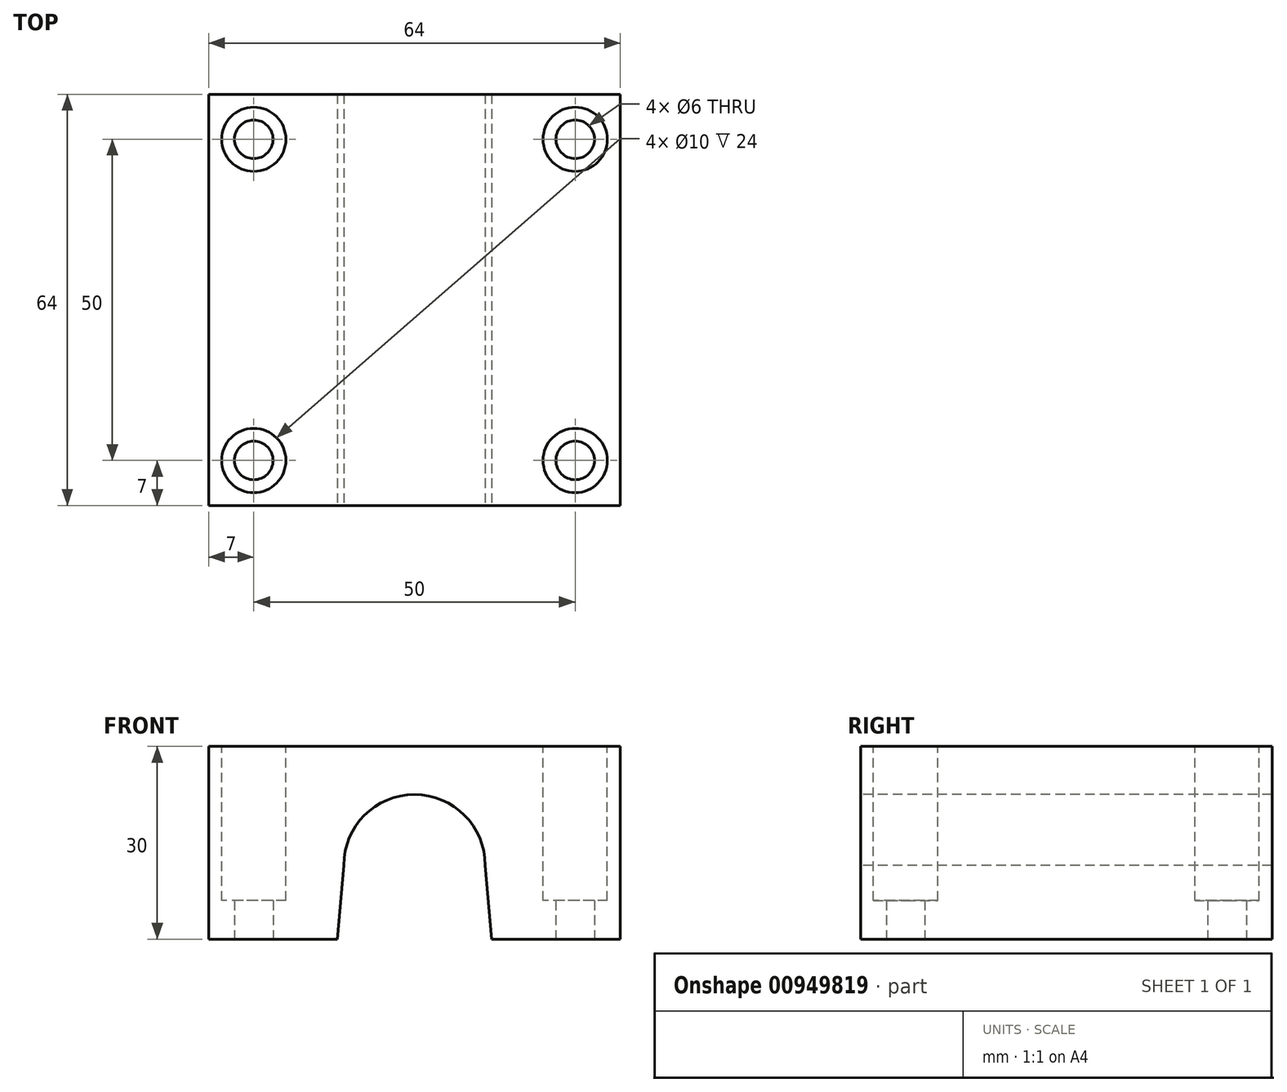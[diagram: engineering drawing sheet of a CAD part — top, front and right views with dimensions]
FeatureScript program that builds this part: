
annotation { "Feature Type Name" : "Feature", "Feature Type Description" : "" }
export const myFeature = defineFeature(function(context is Context, id is Id, definition is map)
    precondition{}
    {
        {
            var Q0;
            Q0=qCreatedBy(makeId("Top.planeOp"),FACE);
            var sketch = newSketch(context, id + "F0", { "sketchPlane" : qUnion([Q0])});
            skLineSegment(sketch, "E0.bottom", {"start": v(32, -32) * mm, "end": v(-32, -32) * mm});
            skLineSegment(sketch, "E0.top", {"start": v(32, 32) * mm, "end": v(-32, 32) * mm});
            skLineSegment(sketch, "E0.left", {"start": v(32, -32) * mm, "end": v(32, 32) * mm});
            skLineSegment(sketch, "E0.right", {"start": v(-32, -32) * mm, "end": v(-32, 32) * mm});
            skPoint(sketch, "E0.middle", {"position": v(0, 0) * mm});
            skLineSegment(sketch, "E1.bottom", {"start": v(-32, -32) * mm, "end": v(-25, -32) * mm});
            skLineSegment(sketch, "E1.top", {"start": v(-32, -25) * mm, "end": v(-25, -25) * mm});
            skLineSegment(sketch, "E1.left", {"start": v(-32, -32) * mm, "end": v(-32, -25) * mm});
            skLineSegment(sketch, "E1.right", {"start": v(-25, -32) * mm, "end": v(-25, -25) * mm});
            skLineSegment(sketch, "E2.bottom", {"start": v(32, -32) * mm, "end": v(25, -32) * mm});
            skLineSegment(sketch, "E2.top", {"start": v(32, -25) * mm, "end": v(25, -25) * mm});
            skLineSegment(sketch, "E2.left", {"start": v(32, -32) * mm, "end": v(32, -25) * mm});
            skLineSegment(sketch, "E2.right", {"start": v(25, -32) * mm, "end": v(25, -25) * mm});
            skLineSegment(sketch, "E3.bottom", {"start": v(32, 32) * mm, "end": v(25, 32) * mm});
            skLineSegment(sketch, "E3.top", {"start": v(32, 25) * mm, "end": v(25, 25) * mm});
            skLineSegment(sketch, "E3.left", {"start": v(32, 32) * mm, "end": v(32, 25) * mm});
            skLineSegment(sketch, "E3.right", {"start": v(25, 32) * mm, "end": v(25, 25) * mm});
            skLineSegment(sketch, "E4.bottom", {"start": v(-32, 32) * mm, "end": v(-25, 32) * mm});
            skLineSegment(sketch, "E4.top", {"start": v(-32, 25) * mm, "end": v(-25, 25) * mm});
            skLineSegment(sketch, "E4.left", {"start": v(-32, 32) * mm, "end": v(-32, 25) * mm});
            skLineSegment(sketch, "E4.right", {"start": v(-25, 32) * mm, "end": v(-25, 25) * mm});
            skCircle(sketch, "E5", {"center": v(-25, -25) * mm, "radius": 3 * mm});
            skCircle(sketch, "E6", {"center": v(25, -25) * mm, "radius": 3 * mm});
            skCircle(sketch, "E7", {"center": v(25, 25) * mm, "radius": 3 * mm});
            skCircle(sketch, "E8", {"center": v(-25, 25) * mm, "radius": 3 * mm});
            skLineSegment(sketch, "E9", {"start": v(-32, -32) * mm, "end": v(-12, -32) * mm});
            skLineSegment(sketch, "E10", {"start": v(32, -32) * mm, "end": v(12, -32) * mm});
            skSolve(sketch);
        }
        {
            var Q0;
            Q0 = qSketchRegion(id + "F0", true);
            var Q1;
            {var subQ18=sQuery(id+"F0.wireOp",EDGE,"E0.bottom");Q1=makeQuery(id+"F0.imprint","IMPRINT",FACE,{"disambiguationData":[TD([[makeQuery(id+"F0.imprint","IMPRINT",EDGE,{"derivedFrom":subQ18}),-1.0]])]});}
            extrude(context, id + "F1", {"entities" : qUnion([Q0, Q1]), "endBound" : BoundingType.SYMMETRIC, "depth" : 30 * mm, "offsetDistance" : 25 * mm});
        }
        {
            var Q0;
            Q0=makeQuery(id+"F1.opExtrude","SWEPT_FACE",FACE,{"disambiguationData":[OSD([sQuery(id+"F0.wireOp",EDGE,"E0.bottom"),sQuery(id+"F0.wireOp",EDGE,"E9"),sQuery(id+"F0.wireOp",EDGE,"E10")])]});
            var sketch = newSketch(context, id + "F2", { "sketchPlane" : qUnion([Q0])});
            skLineSegment(sketch, "E11", {"start": v(-32, -15) * mm, "end": v(-12, -15) * mm});
            skLineSegment(sketch, "E12", {"start": v(-12, -15) * mm, "end": v(12, -15) * mm});
            skLineSegment(sketch, "E13", {"start": v(12, -15) * mm, "end": v(32, -15) * mm});
            skLineSegment(sketch, "E14", {"start": v(0, -15) * mm, "end": v(0, 8) * mm});
            skLineSegment(sketch, "E15", {"start": v(0, 8) * mm, "end": v(0, -3.5) * mm});
            skCircle(sketch, "E16", {"center": v(0, -3.5) * mm, "radius": 11 * mm});
            skLineSegment(sketch, "E17", {"start": v(0, -3.5) * mm, "end": v(-11, -3.5) * mm});
            skLineSegment(sketch, "E18", {"start": v(0, -3.5) * mm, "end": v(11, -3.5) * mm});
            skLineSegment(sketch, "E19", {"start": v(-11, -3.5) * mm, "end": v(-12, -15) * mm});
            skLineSegment(sketch, "E20", {"start": v(11, -3.5) * mm, "end": v(12, -15) * mm});
            skSolve(sketch);
        }
        {
            var Q0;
            {var subQ0=sQuery(id+"F2.wireOp",EDGE,"E19");Q0=makeQuery(id+"F2.imprint","IMPRINT",FACE,{"disambiguationData":[TD([[makeQuery(id+"F2.imprint","IMPRINT",EDGE,{"derivedFrom":subQ0}),1.0]])]});}
            var Q1;
            {var subQ0=sQuery(id+"F2.wireOp",EDGE,"E17");Q1=makeQuery(id+"F2.imprint","IMPRINT",FACE,{"disambiguationData":[TD([[makeQuery(id+"F2.imprint","IMPRINT",EDGE,{"derivedFrom":subQ0}),1.0]])]});}
            var Q2;
            {var subQ0=sQuery(id+"F2.wireOp",EDGE,"E18");Q2=makeQuery(id+"F2.imprint","IMPRINT",FACE,{"disambiguationData":[TD([[makeQuery(id+"F2.imprint","IMPRINT",EDGE,{"derivedFrom":subQ0}),-1.0]])]});}
            var Q3;
            {var subQ0=sQuery(id+"F2.wireOp",EDGE,"E20");Q3=makeQuery(id+"F2.imprint","IMPRINT",FACE,{"disambiguationData":[TD([[makeQuery(id+"F2.imprint","IMPRINT",EDGE,{"derivedFrom":subQ0}),-1.0]])]});}
            var Q4;
            {var subQ0=sQuery(id+"F2.wireOp",EDGE,"E18");Q4=makeQuery(id+"F2.imprint","IMPRINT",FACE,{"disambiguationData":[TD([[makeQuery(id+"F2.imprint","IMPRINT",EDGE,{"derivedFrom":subQ0}),1.0]])]});}
            var Q5;
            {var subQ0=sQuery(id+"F2.wireOp",EDGE,"E17");Q5=makeQuery(id+"F2.imprint","IMPRINT",FACE,{"disambiguationData":[TD([[makeQuery(id+"F2.imprint","IMPRINT",EDGE,{"derivedFrom":subQ0}),-1.0]])]});}
            extrude(context, id + "F3", {"entities" : qUnion([Q0, Q1, Q2, Q3, Q4, Q5]), "operationType" : NewBodyOperationType.REMOVE, "oppositeDirection" : true, "depth" : 64 * mm, "offsetDistance" : 25 * mm});
        }
        {
            var Q0;
            Q0=makeQuery(id+"F1.opExtrude","CAP_FACE",FACE,{"disambiguationData":[OSD([sQuery(id+"F0.wireOp",EDGE,"E0.bottom"),sQuery(id+"F0.wireOp",EDGE,"E0.top"),sQuery(id+"F0.wireOp",EDGE,"E0.left"),sQuery(id+"F0.wireOp",EDGE,"E0.right"),sQuery(id+"F0.wireOp",EDGE,"E1.left"),sQuery(id+"F0.wireOp",EDGE,"E2.left"),sQuery(id+"F0.wireOp",EDGE,"E3.bottom"),sQuery(id+"F0.wireOp",EDGE,"E3.left"),sQuery(id+"F0.wireOp",EDGE,"E4.bottom"),sQuery(id+"F0.wireOp",EDGE,"E4.left"),sQuery(id+"F0.wireOp",EDGE,"E5"),sQuery(id+"F0.wireOp",EDGE,"E6"),sQuery(id+"F0.wireOp",EDGE,"E7"),sQuery(id+"F0.wireOp",EDGE,"E8"),sQuery(id+"F0.wireOp",EDGE,"E9"),sQuery(id+"F0.wireOp",EDGE,"E10")])],"isStart":false});
            var sketch = newSketch(context, id + "F4", { "sketchPlane" : qUnion([Q0])});
            skCircle(sketch, "E21", {"center": v(-25, 25) * mm, "radius": 5 * mm});
            skCircle(sketch, "E22", {"center": v(25, 25) * mm, "radius": 5 * mm});
            skCircle(sketch, "E23", {"center": v(-25, -25) * mm, "radius": 5 * mm});
            skCircle(sketch, "E24", {"center": v(25, -25) * mm, "radius": 5 * mm});
            skSolve(sketch);
        }
        {
            var Q0;
            Q0=makeQuery(id+"F4.imprint","IMPRINT",FACE,{"disambiguationData":[TD([[makeQuery(id+"F4.imprint","IMPRINT",EDGE,{"derivedFrom":makeQuery(id+"F1.opExtrude","CAP_EDGE",EDGE,{"disambiguationData":[OSD([sQuery(id+"F0.wireOp",EDGE,"E5")])],"isStart":false})}),1.0]])]});
            var Q1;
            Q1=makeQuery(id+"F4.imprint","IMPRINT",FACE,{"disambiguationData":[TD([[makeQuery(id+"F4.imprint","IMPRINT",EDGE,{"derivedFrom":makeQuery(id+"F1.opExtrude","CAP_EDGE",EDGE,{"disambiguationData":[OSD([sQuery(id+"F0.wireOp",EDGE,"E6")])],"isStart":false})}),1.0]])]});
            var Q2;
            Q2=makeQuery(id+"F4.imprint","IMPRINT",FACE,{"disambiguationData":[TD([[makeQuery(id+"F4.imprint","IMPRINT",EDGE,{"derivedFrom":makeQuery(id+"F1.opExtrude","CAP_EDGE",EDGE,{"disambiguationData":[OSD([sQuery(id+"F0.wireOp",EDGE,"E7")])],"isStart":false})}),1.0]])]});
            var Q3;
            Q3=makeQuery(id+"F4.imprint","IMPRINT",FACE,{"disambiguationData":[TD([[makeQuery(id+"F4.imprint","IMPRINT",EDGE,{"derivedFrom":makeQuery(id+"F1.opExtrude","CAP_EDGE",EDGE,{"disambiguationData":[OSD([sQuery(id+"F0.wireOp",EDGE,"E8")])],"isStart":false})}),1.0]])]});
            var Q4;
            Q4=makeQuery(id+"F4.imprint","IMPRINT",FACE,{"disambiguationData":[TD([[makeQuery(id+"F4.imprint","IMPRINT",EDGE,{"derivedFrom":sQuery(id+"F4.wireOp",EDGE,"E23")}),1.0]])]});
            var Q5;
            Q5=makeQuery(id+"F4.imprint","IMPRINT",FACE,{"disambiguationData":[TD([[makeQuery(id+"F4.imprint","IMPRINT",EDGE,{"derivedFrom":sQuery(id+"F4.wireOp",EDGE,"E21")}),1.0]])]});
            var Q6;
            Q6=makeQuery(id+"F4.imprint","IMPRINT",FACE,{"disambiguationData":[TD([[makeQuery(id+"F4.imprint","IMPRINT",EDGE,{"derivedFrom":sQuery(id+"F4.wireOp",EDGE,"E22")}),1.0]])]});
            var Q7;
            Q7=makeQuery(id+"F4.imprint","IMPRINT",FACE,{"disambiguationData":[TD([[makeQuery(id+"F4.imprint","IMPRINT",EDGE,{"derivedFrom":sQuery(id+"F4.wireOp",EDGE,"E24")}),1.0]])]});
            extrude(context, id + "F5", {"entities" : qUnion([Q0, Q1, Q2, Q3, Q4, Q5, Q6, Q7]), "operationType" : NewBodyOperationType.REMOVE, "oppositeDirection" : true, "depth" : 24 * mm, "offsetDistance" : 25 * mm});
        }
    });
